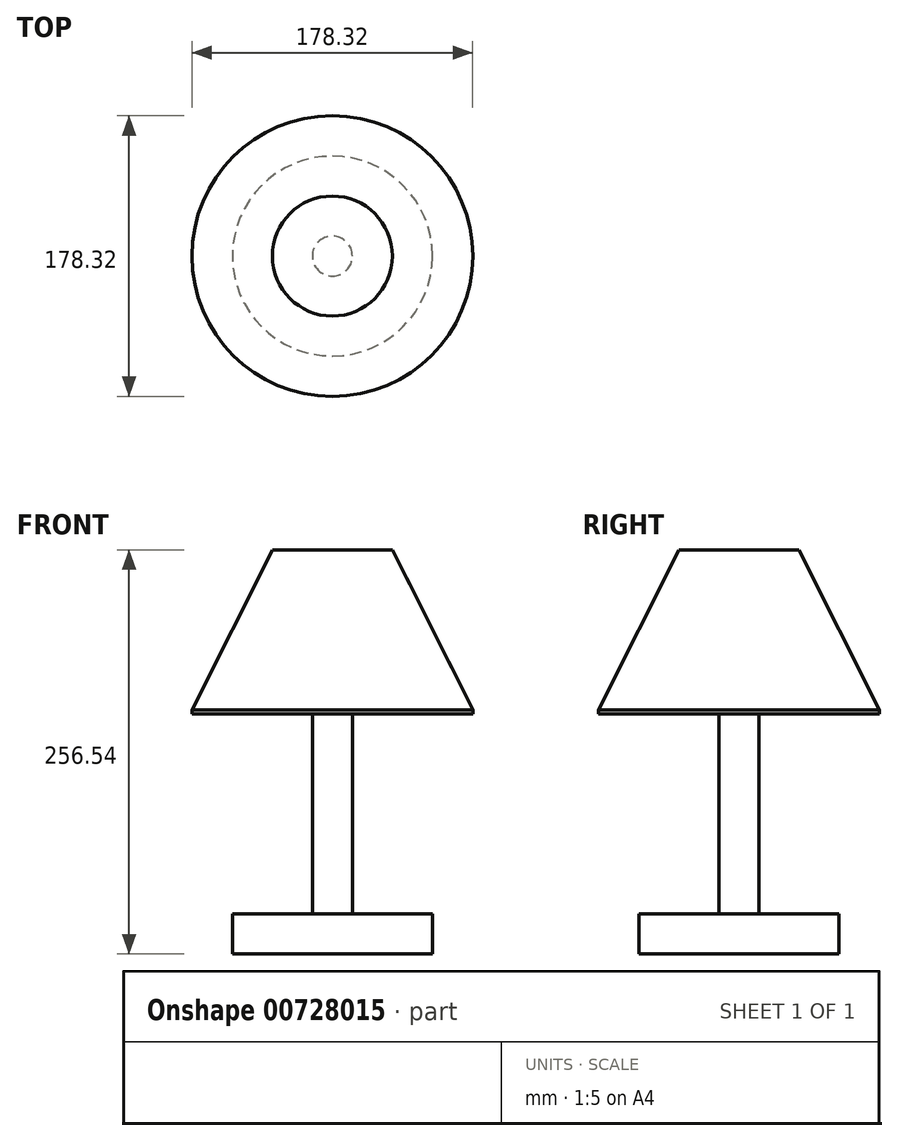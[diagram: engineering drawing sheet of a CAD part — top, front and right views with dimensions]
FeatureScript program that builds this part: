
annotation { "Feature Type Name" : "Feature", "Feature Type Description" : "" }
export const myFeature = defineFeature(function(context is Context, id is Id, definition is map)
    precondition{}
    {
        {
            var Q0;
            Q0=qCreatedBy(makeId("Top.planeOp"),FACE);
            var sketch = newSketch(context, id + "F0", { "sketchPlane" : qUnion([Q0])});
            skCircle(sketch, "E0", {"center": v(0, 0) * mm, "radius": 63.5 * mm});
            skSolve(sketch);
        }
        {
            var Q0;
            Q0=makeQuery(id+"F0.imprint","IMPRINT",FACE,{"disambiguationData":[TD([[makeQuery(id+"F0.imprint","IMPRINT",EDGE,{"derivedFrom":sQuery(id+"F0.wireOp",EDGE,"E0")}),1.0]])]});
            extrude(context, id + "F1", {"entities" : qUnion([Q0]), "depth" : 25.4 * mm, "offsetDistance" : 25.4 * mm});
        }
        {
            var Q0;
            Q0=makeQuery(id+"F1.opExtrude","CAP_FACE",FACE,{"disambiguationData":[OSD([sQuery(id+"F0.wireOp",EDGE,"E0")])],"isStart":false});
            var sketch = newSketch(context, id + "F2", { "sketchPlane" : qUnion([Q0])});
            skCircle(sketch, "E1", {"center": v(0, 0) * mm, "radius": 12.7 * mm});
            skSolve(sketch);
        }
        {
            var Q0;
            Q0=makeQuery(id+"F2.imprint","IMPRINT",FACE,{"disambiguationData":[TD([[makeQuery(id+"F2.imprint","IMPRINT",EDGE,{"derivedFrom":sQuery(id+"F2.wireOp",EDGE,"E1")}),1.0]])]});
            extrude(context, id + "F3", {"entities" : qUnion([Q0]), "operationType" : NewBodyOperationType.ADD, "depth" : 127 * mm, "offsetDistance" : 25.4 * mm});
        }
        {
            var Q0;
            Q0=makeQuery(id+"F3.opExtrude","CAP_FACE",FACE,{"disambiguationData":[OSD([sQuery(id+"F2.wireOp",EDGE,"E1")])],"isStart":false});
            var sketch = newSketch(context, id + "F4", { "sketchPlane" : qUnion([Q0])});
            skCircle(sketch, "E2", {"center": v(0, 0) * mm, "radius": 89.16 * mm});
            skSolve(sketch);
        }
        {
            var Q0;
            Q0=makeQuery(id+"F4.imprint","IMPRINT",FACE,{"disambiguationData":[TD([[makeQuery(id+"F4.imprint","IMPRINT",EDGE,{"derivedFrom":sQuery(id+"F4.wireOp",EDGE,"E2")}),1.0]])]});
            var Q1;
            Q1=makeQuery(id+"F4.imprint","IMPRINT",FACE,{"disambiguationData":[TD([[makeQuery(id+"F4.imprint","IMPRINT",EDGE,{"derivedFrom":makeQuery(id+"F3.opExtrude","CAP_EDGE",EDGE,{"disambiguationData":[OSD([sQuery(id+"F2.wireOp",EDGE,"E1")])],"isStart":false})}),1.0]])]});
            extrude(context, id + "F5", {"entities" : qUnion([Q0, Q1]), "operationType" : NewBodyOperationType.ADD, "depth" : 2.54 * mm, "offsetDistance" : 25.4 * mm});
        }
        {
            var Q0;
            Q0=makeQuery(id+"F5.opExtrude","CAP_FACE",FACE,{"disambiguationData":[OSD([sQuery(id+"F4.wireOp",EDGE,"E2")])],"isStart":false});
            cPlane(context, id + "F6", {"entities" : qUnion([Q0]), "cplaneType" : CPlaneType.OFFSET, "offset" : 101.6 * mm, "width" : 152.4 * mm, "height" : 152.4 * mm});
        }
        {
            var Q0;
            Q0=qCreatedBy(id+"F6.planeOp",FACE);
            var sketch = newSketch(context, id + "F7", { "sketchPlane" : qUnion([Q0])});
            skCircle(sketch, "E3", {"center": v(0, 0) * mm, "radius": 38.1 * mm});
            skSolve(sketch);
        }
        {
            var Q1;
            Q1=makeQuery(id+"F5.opExtrude","CAP_FACE",FACE,{"disambiguationData":[OSD([sQuery(id+"F4.wireOp",EDGE,"E2")])],"isStart":false});
            var Q2;
            Q2=makeQuery(id+"F7.imprint","IMPRINT",FACE,{"disambiguationData":[TD([[makeQuery(id+"F7.imprint","IMPRINT",EDGE,{"derivedFrom":sQuery(id+"F7.wireOp",EDGE,"E3")}),1.0]])]});
            loft(context, id + "F8", {"operationType" : NewBodyOperationType.ADD, "sheetProfilesArray" : [{ "sheetProfileEntities" : qUnion([Q1]) }, { "sheetProfileEntities" : qUnion([Q2]) }]});
        }
    });
